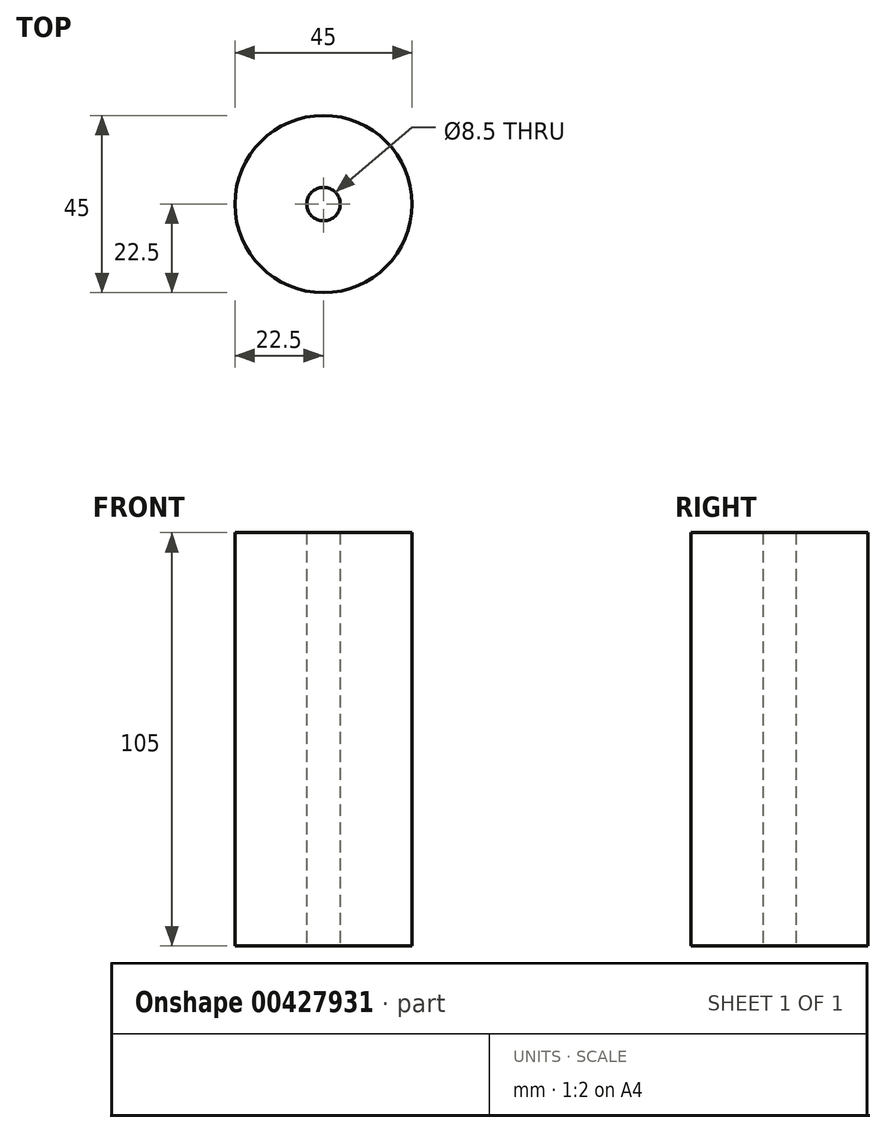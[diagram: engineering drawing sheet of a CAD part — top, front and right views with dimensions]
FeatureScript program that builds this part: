
annotation { "Feature Type Name" : "Feature", "Feature Type Description" : "" }
export const myFeature = defineFeature(function(context is Context, id is Id, definition is map)
    precondition{}
    {
        {
            var Q0;
            Q0=qCreatedBy(makeId("Top.planeOp"),FACE);
            var sketch = newSketch(context, id + "F0", { "sketchPlane" : qUnion([Q0])});
            skCircle(sketch, "E0", {"center": v(0, 0) * mm, "radius": 4.25 * mm});
            skCircle(sketch, "E1", {"center": v(0, 0) * mm, "radius": 22.5 * mm});
            skSolve(sketch);
        }
        {
            var Q0;
            Q0 = qSketchRegion(id + "F0", true);
            extrude(context, id + "F1", {"entities" : qUnion([Q0]), "depth" : 105 * mm});
        }
    });
